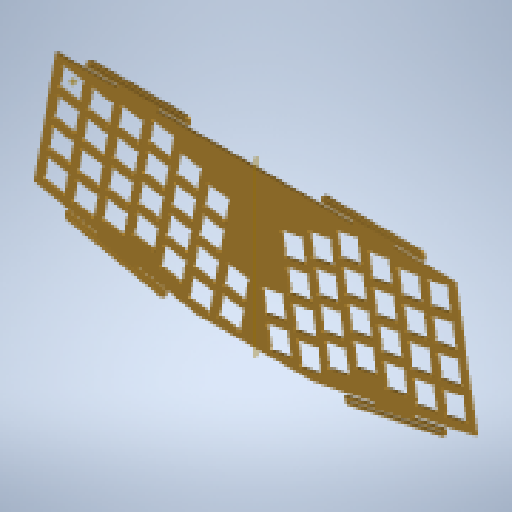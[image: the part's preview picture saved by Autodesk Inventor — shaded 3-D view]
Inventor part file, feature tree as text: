
AUTODESK INVENTOR PART (.ipt)
format: ipt  version: 2023 (Build 270158000, 158)  size: 1,212,928 bytes
history: native  units: mm
features: reference x11, other x6, sketch x5, extrude x3, plane x1, mirror x1, projected_geometry x1
ambient origin geometry x8: Origin, YZ Plane, XZ Plane, XY Plane, X Axis, Y Axis, Z Axis, Center Point
bodies: Body1 (feature_tree)
feature tree (28):
  extrude  "Extrusion2"  Depth=2.0mm
  extrude  "Extrusion3"  Depth=2.0mm
  sketch  "Sketch3"  dims[d11=13.0mm]
  other  "Work Point1"
  sketch  "Sketch Driven Pattern1"  dims[d1=2.0mm d2=2.0mm]
  plane  "Work Plane1"
  mirror  "Mirror1"
  extrude  "Extrusion4"  Depth=1.5mm TaperAngle=0.0deg
  sketch  "Sketch1"  dims[d3=2.0mm d4=2.0mm]
  reference  "Reference1"
  reference  "Reference2"
  reference  "Reference3"
  reference  "Reference4"
  reference  "Reference5"
  reference  "Reference6"
  reference  "Reference7"
  sketch  "Sketch2"  dims[d5=2.0mm d9=1.5mm d10=0.0mm]
  reference  "Reference8"
  reference  "Reference9"
  reference  "Reference10"
  reference  "Reference11"
  sketch  "Sketch4"  dims[d12=0.47mm d13=2.0mm d14=2.0mm d15=2.0mm d16=2.0mm d17=1.5mm d18=0.0mm d19=1.5mm d20=1.5mm d21=2.0mm d22=20.0mm d23=20.0mm d24=25.0mm d25=40.0mm d26=1.5mm d27=1.5mm d28=2.0mm d29=20.0mm d30=20.0mm d31=25.0mm d32=40.0mm d33=1.5mm d34=0.0mm d35=0.5mm d36=0.872665mm]
  projected_geometry  "Projected Loop1"
  other  "<userpath>\Documents\Inventor\atreus-52\Assembly.iam"
  other  "Assembly.iam"
  other  "atreus52_hotswap:1"
  other  "asm_mx_asm_PLATE:1"
  other  "asm_mx_asm_PLATE:2"
